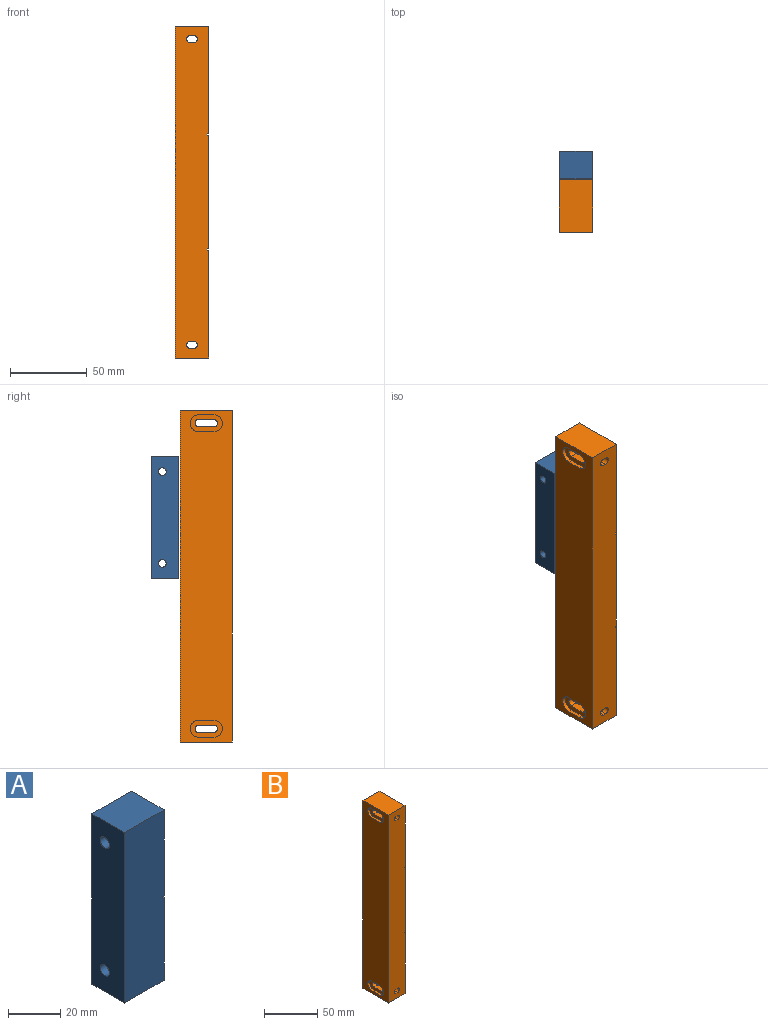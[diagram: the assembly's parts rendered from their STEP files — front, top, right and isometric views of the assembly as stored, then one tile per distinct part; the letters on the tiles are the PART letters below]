
ASSEMBLY  parts=2 mates=1
PART A: 12 faces, bbox 21.5x17.7x80 mm
  f0: plane 38.87x17.7mm, normal (1,0,0), area 668.4mm2, adj f1,f2,f6,f7,f9
  f1: plane 80x21.46mm, normal (0,1,0), area 1716mm2, adj f0,f3,f4,f5,f6,f9,f10,f11
  f2: plane 80x21.46mm, normal (0,-1,0), area 1716mm2, adj f0,f3,f4,f5,f6,f9,f10,f11
  f3: plane 80x17.7mm, normal (-1,0,0), area 1377mm2, adj f1,f2,f5,f6,f7,f8
  f4: plane 40.14x17.7mm, normal (1,0,0), area 690.9mm2, adj f1,f2,f5,f8,f10
  f5: plane 21.46x17.7mm, normal (0,0,1), area 380mm2, adj f1,f2,f3,f4
  f6: plane 21.46x17.7mm, normal (0,0,-1), area 380mm2, adj f0,f1,f2,f3
  f7: cylinder r=2.5mm len=21.46mm, axis (-1,0,0), area 337.1mm2, adj f0,f3
  f8: cylinder r=2.5mm len=21.46mm, axis (-1,0,0), area 337.1mm2, adj f3,f4
  f9: plane 17.7x1mm, normal (0,0,1), area 17.7mm2, adj f0,f1,f2,f11
  f10: plane 17.7x1mm, normal (0,0,-1), area 17.7mm2, adj f1,f2,f4,f11
  f11: plane 17.7x1mm, normal (1,0,0), area 17.7mm2, adj f1,f2,f9,f10
PART B: 52 faces, bbox 22x34x216.7 mm
  f0: cylinder r=2.4mm len=31.46mm, axis (0,1,0), area 144.9mm2, adj f5,f21,f22,f23,f48,f49,f50,f51
  f1: cylinder r=2.4mm len=31.46mm, axis (0,1,0), area 144.9mm2, adj f5,f21,f22,f23,f44,f45,f46,f47
  f2: plane 70.35x34mm, normal (1,0,0), area 2326.4mm2, adj f4,f5,f8,f34,f40,f41,f42,f43
  f3: plane 74x34mm, normal (1,0,0), area 2516mm2, adj f4,f5,f30,f33
  f4: plane 216.7x22mm, normal (0,1,0), area 4592.2mm2, adj f2,f3,f6,f7,f8,f9,f20,f24
  f5: plane 216.7x22mm, normal (0,-1,0), area 4708.1mm2, adj f0,f1,f2,f3,f6,f7,f8,f9
  f6: plane 216.7x34mm, normal (-1,0,0), area 6957.7mm2, adj f4,f5,f8,f9,f10,f11,f12,f13
  f7: plane 70.35x34mm, normal (1,0,0), area 2326.4mm2, adj f4,f5,f9,f31,f44,f45,f46,f47
  f8: plane 34x22mm, normal (0,0,1), area 748mm2, adj f2,f4,f5,f6
  f9: plane 34x22mm, normal (0,0,-1), area 748mm2, adj f4,f5,f6,f7
  f10: plane 10x2.54mm, normal (0,0,1), area 25.4mm2, adj f6,f11,f13,f14
  f11: cylinder r=5.5mm len=11mm, axis (-1,0,0), area 43.9mm2, adj f6,f10,f12,f14
  f12: plane 10x2.54mm, normal (0,0,-1), area 25.4mm2, adj f6,f11,f13,f14
  f13: cylinder r=5.5mm len=11mm, axis (-1,0,0), area 43.9mm2, adj f6,f10,f12,f14
  f14: plane 21x11mm, normal (-1,0,0), area 139.5mm2, adj f10,f11,f12,f13,f48,f49,f50,f51
  f15: plane 10x2.54mm, normal (0,0,-1), area 25.4mm2, adj f6,f16,f18,f19
  f16: cylinder r=5.5mm len=11mm, axis (-1,0,0), area 43.9mm2, adj f6,f15,f17,f19
  f17: plane 10x2.54mm, normal (0,0,1), area 25.4mm2, adj f6,f16,f18,f19
  f18: cylinder r=5.5mm len=11mm, axis (-1,0,0), area 43.9mm2, adj f6,f15,f17,f19
  f19: plane 21x11mm, normal (-1,0,0), area 139.5mm2, adj f15,f16,f17,f18,f36,f37,f38,f39
  f20: cylinder r=5.25mm len=10.5mm, axis (0,1,0), area 83.8mm2, adj f4,f21
  f21: plane 10.5x10.5mm, normal (0,1,0), area 57.9mm2, adj f0,f1,f20,f22,f23
  f22: plane 31.46x2.2mm, normal (0,0,1), area 69.2mm2, adj f0,f1,f5,f21
  f23: plane 31.46x2.2mm, normal (0,0,-1), area 69.2mm2, adj f0,f1,f5,f21
  f24: cylinder r=5.25mm len=10.5mm, axis (0,1,0), area 83.8mm2, adj f4,f25
  f25: plane 10.5x10.5mm, normal (0,1,0), area 57.9mm2, adj f24,f26,f27,f28,f29
  f26: plane 31.46x2.2mm, normal (0,0,-1), area 69.2mm2, adj f5,f25,f27,f29
  f27: cylinder r=2.4mm len=31.46mm, axis (0,1,0), area 144.9mm2, adj f5,f25,f26,f28,f40,f41,f42,f43
  f28: plane 31.46x2.2mm, normal (0,0,1), area 69.2mm2, adj f5,f25,f27,f29
  f29: cylinder r=2.4mm len=31.46mm, axis (0,1,0), area 144.9mm2, adj f5,f25,f26,f28,f36,f37,f38,f39
  f30: plane 34x1mm, normal (0,0,-1), area 34mm2, adj f3,f4,f5,f32
  f31: plane 34x1mm, normal (0,0,1), area 34mm2, adj f4,f5,f7,f32
  f32: plane 34x1mm, normal (1,0,0), area 34mm2, adj f4,f5,f30,f31
  f33: plane 34x1mm, normal (0,0,1), area 34mm2, adj f3,f4,f5,f35
  f34: plane 34x1mm, normal (0,0,-1), area 34mm2, adj f2,f4,f5,f35
  f35: plane 34x1mm, normal (1,0,0), area 34mm2, adj f4,f5,f33,f34
  f36: cylinder r=2.38mm len=7.08mm, axis (-1,0,0), area 43.4mm2, adj f19,f29,f37,f39
  f37: plane 10x7.08mm, normal (0,0,1), area 70.8mm2, adj f19,f29,f36,f38
  f38: cylinder r=2.38mm len=7.08mm, axis (-1,0,0), area 43.4mm2, adj f19,f29,f37,f39
  f39: plane 10x7.08mm, normal (0,0,-1), area 70.8mm2, adj f19,f29,f36,f38
  f40: plane 10x9.62mm, normal (0,0,-1), area 96.2mm2, adj f2,f27,f41,f43
  f41: cylinder r=2.38mm len=9.62mm, axis (-1,0,0), area 62.5mm2, adj f2,f27,f40,f42
  f42: plane 10x9.62mm, normal (0,0,1), area 96.2mm2, adj f2,f27,f41,f43
  f43: cylinder r=2.38mm len=9.62mm, axis (-1,0,0), area 62.5mm2, adj f2,f27,f40,f42
  f44: cylinder r=2.38mm len=9.62mm, axis (-1,0,0), area 62.5mm2, adj f1,f7,f45,f47
  f45: plane 10x9.62mm, normal (0,0,-1), area 96.2mm2, adj f1,f7,f44,f46
  f46: cylinder r=2.38mm len=9.62mm, axis (-1,0,0), area 62.5mm2, adj f1,f7,f45,f47
  f47: plane 10x9.62mm, normal (0,0,1), area 96.2mm2, adj f1,f7,f44,f46
  f48: plane 10x7.08mm, normal (0,0,1), area 70.8mm2, adj f0,f14,f49,f51
  f49: cylinder r=2.38mm len=7.08mm, axis (-1,0,0), area 43.4mm2, adj f0,f14,f48,f50
  f50: plane 10x7.08mm, normal (0,0,-1), area 70.8mm2, adj f0,f14,f49,f51
  f51: cylinder r=2.38mm len=7.08mm, axis (-1,0,0), area 43.4mm2, adj f0,f14,f48,f50
PLACE A t=(0.65,35.9,7.73)mm
PLACE B t=(0.65,-16.8,-98.77)mm fixed
MATE slider A.f5 <-> B.f8  axis (0,0,1) through (0.65,18.2,87.73)mm
